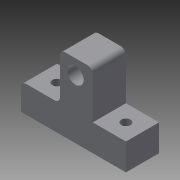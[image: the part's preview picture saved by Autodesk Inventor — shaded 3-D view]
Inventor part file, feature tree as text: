
AUTODESK INVENTOR PART (.ipt)
format: ipt  version: 2015 (Build 190159000, 159)  size: 180,736 bytes
history: native  units: in
note: dims shown in document units (in); Inventor stores cm internally (conversion verified against a paired STEP export)
features: other x7, extrude x7, sketch x7, plane x4, projected_geometry x4, fillet x1
ambient origin geometry x8: Origin, YZ Plane, XZ Plane, XY Plane, X Axis, Y Axis, Z Axis, Center Point
bodies: Body1 (feature_tree)
feature tree (30):
  other  "dc_motor_mount_2012"
  other  "A_2"
  other  "A_3"
  other  "A_4"
  other  "FRONT"
  other  "TOP"
  other  "RIGHT"
  plane  "Work Plane6"
  extrude  "Extrusion1"  Depth=0.5in
  plane  "Work Plane5"
  extrude  "Extrusion2"  Depth=0.5in TaperAngle=0.0deg
  plane  "Work Plane8"
  extrude  "Extrusion3"  Depth=0.3937in TaperAngle=0.0deg
  extrude  "Extrusion4"  Depth=0.0787in
  extrude  "Extrusion5"  Depth=0.3937in
  fillet  "Fillet4"  Radius=0.3937in
  plane  "Work Plane9"
  extrude  "Extrusion6"  [1 undecoded]
  extrude  "Extrusion7"  [1 undecoded]
  sketch  "Sketch1"  dims[d0=0.5in d1=0.0in d2=0.2441in]
  sketch  "Sketch2"  dims[d3=0.5in d4=0.0in d7=0.5in d8=0.0in]
  sketch  "Sketch3"  dims[d12=0.3937in d13=0.0in d14=0.3937in d15=0.0in]
  sketch  "Sketch4"  dims[d16=0.0787in d18=0.1406in]
  projected_geometry  "Projected Loop1"
  sketch  "Sketch5"  dims[d19=0.3937in d20=0.0in d21=0.1406in d22=0.3937in d23=0.0in]
  projected_geometry  "Projected Loop2"
  sketch  "Sketch6"
  projected_geometry  "Projected Loop3"
  sketch  "Sketch7"
  projected_geometry  "Projected Loop4"
note: 2 required parameter values undecoded (feature->parameter linkage not recoverable at this tier; creation-order binding heuristic only, values carry confidence <= 0.55)
